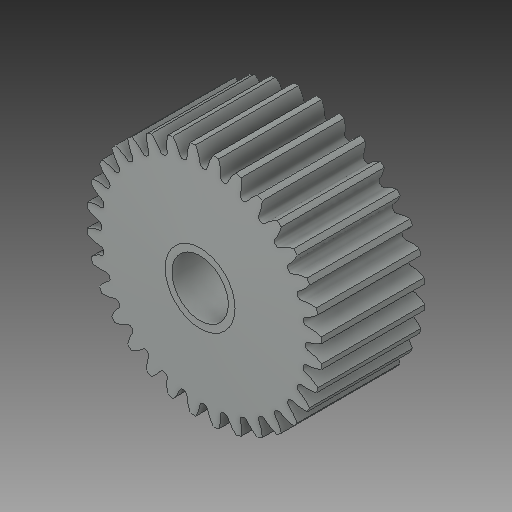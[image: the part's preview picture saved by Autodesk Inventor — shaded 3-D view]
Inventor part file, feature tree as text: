
AUTODESK INVENTOR PART (.ipt)
format: ipt  version: 2018 (Build 220112000, 112)  size: 499,200 bytes
history: native  units: in
note: dims shown in document units (in); Inventor stores cm internally (conversion verified against a paired STEP export)
features: mirror x1
ambient origin geometry x8: Origin, YZ Plane, XZ Plane, XY Plane, X Axis, Y Axis, Z Axis, Center Point
bodies: Solid1 (feature_tree)
feature tree (1):
  mirror  "Mirror1"
